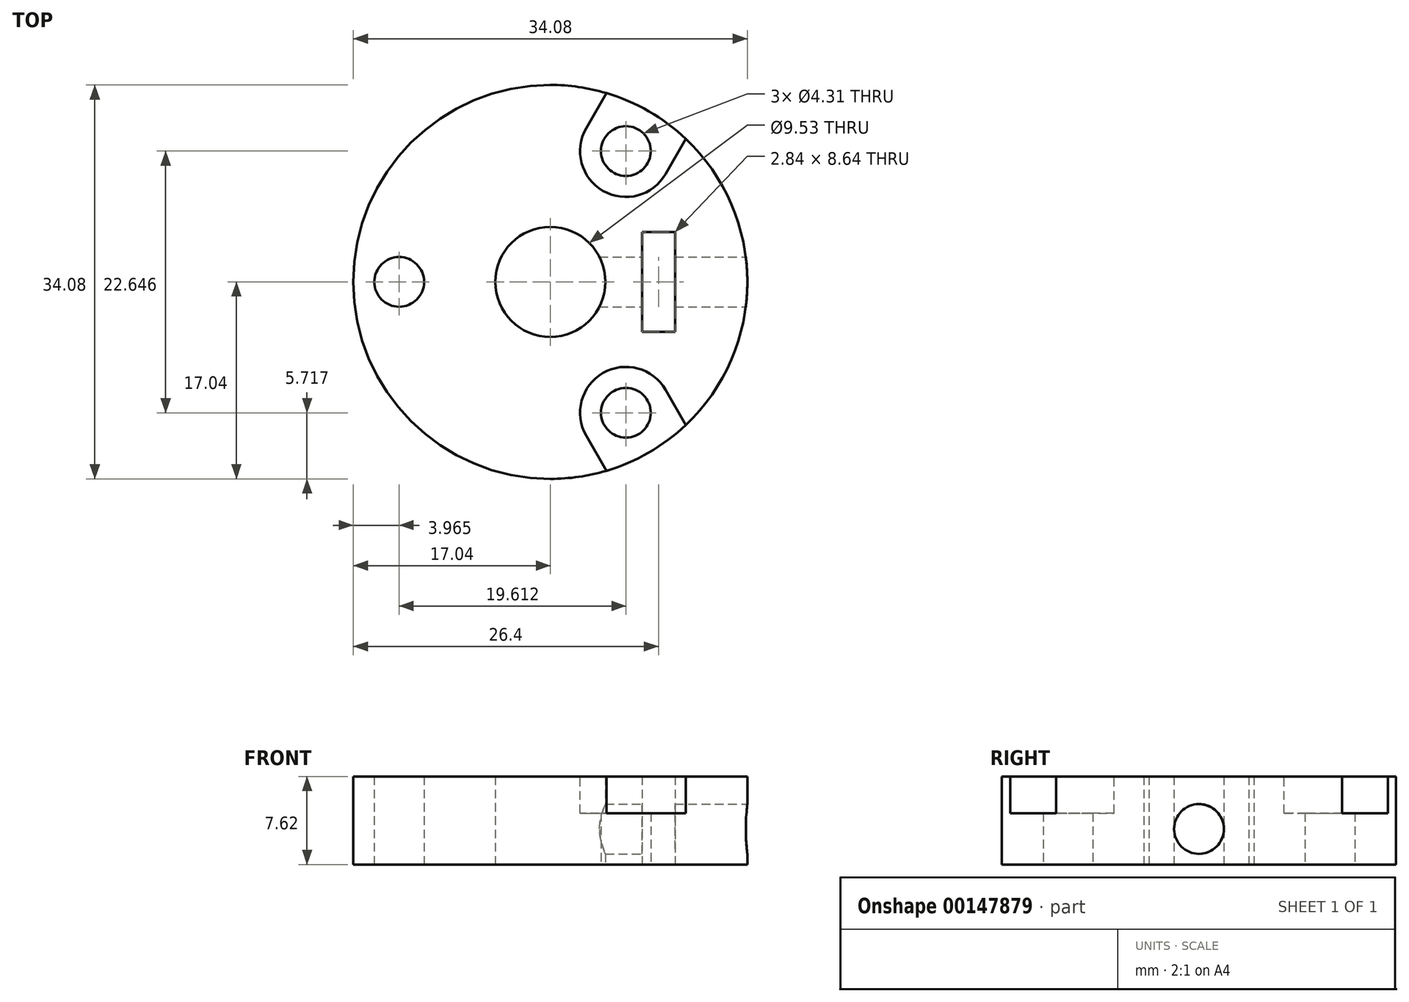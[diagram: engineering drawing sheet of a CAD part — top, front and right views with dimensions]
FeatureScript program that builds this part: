
annotation { "Feature Type Name" : "Feature", "Feature Type Description" : "" }
export const myFeature = defineFeature(function(context is Context, id is Id, definition is map)
    precondition{}
    {
        {
            var Q0;
            Q0=qCreatedBy(makeId("Top.planeOp"),FACE);
            var sketch = newSketch(context, id + "F0", { "sketchPlane" : qUnion([Q0])});
            skCircle(sketch, "E0", {"center": v(0, 0) * mm, "radius": 4.76 * mm});
            skCircle(sketch, "E1.cCircle", {"center": v(0, 0) * mm, "radius": 6.54 * mm, "construction": true});
            skLineSegment(sketch, "E1.0", {"start": v(6.54, 11.32) * mm, "end": v(6.54, -11.32) * mm, "construction": true});
            skLineSegment(sketch, "E1.1", {"start": v(6.54, -11.32) * mm, "end": v(-13.07, 0) * mm, "construction": true});
            skLineSegment(sketch, "E1.2", {"start": v(-13.07, 0) * mm, "end": v(6.54, 11.32) * mm, "construction": true});
            skCircle(sketch, "E2", {"center": v(-13.07, 0) * mm, "radius": 2.15 * mm});
            skCircle(sketch, "E3", {"center": v(6.54, -11.32) * mm, "radius": 2.15 * mm});
            skCircle(sketch, "E4", {"center": v(6.54, 11.32) * mm, "radius": 2.15 * mm});
            skLineSegment(sketch, "E5", {"start": v(4.76, 0) * mm, "end": v(7.94, 0) * mm, "construction": true});
            skLineSegment(sketch, "E6.bottom", {"start": v(7.94, -4.32) * mm, "end": v(10.78, -4.32) * mm});
            skLineSegment(sketch, "E6.top", {"start": v(7.94, 4.32) * mm, "end": v(10.78, 4.32) * mm});
            skLineSegment(sketch, "E6.left", {"start": v(7.94, -4.32) * mm, "end": v(7.94, 4.32) * mm});
            skLineSegment(sketch, "E6.right", {"start": v(10.78, -4.32) * mm, "end": v(10.78, 4.32) * mm});
            skCircle(sketch, "E7", {"center": v(6.54, -11.32) * mm, "radius": 7.14 * mm, "construction": true});
            skPoint(sketch, "E8", {"position": v(6.54, 0) * mm});
            skCircle(sketch, "E9", {"center": v(-13.07, 0) * mm, "radius": 3.97 * mm, "construction": true});
            skLineSegment(sketch, "E10.bottom", {"start": v(-17.04, -17.04) * mm, "end": v(17.04, -17.04) * mm});
            skLineSegment(sketch, "E10.top", {"start": v(-17.04, 17.04) * mm, "end": v(17.04, 17.04) * mm});
            skLineSegment(sketch, "E10.left", {"start": v(-17.04, -17.04) * mm, "end": v(-17.04, 17.04) * mm});
            skLineSegment(sketch, "E10.right", {"start": v(17.04, -17.04) * mm, "end": v(17.04, 17.04) * mm});
            skSolve(sketch);
        }
        {
            var Q0;
            Q0=qSketchRegion(id+"F0",true);
            extrude(context, id + "F1", {"entities" : qUnion([Q0]), "depth" : 7.62 * mm});
        }
        {
            var Q0;
            Q0=makeQuery(id+"F1.opExtrude","SWEPT_FACE",FACE,{"disambiguationData":[OSD([sQuery(id+"F0.wireOp",EDGE,"E10.right")])]});
            var sketch = newSketch(context, id + "F2", { "sketchPlane" : qUnion([Q0])});
            skCircle(sketch, "E11", {"center": v(0, 3.07) * mm, "radius": 2.15 * mm});
            skCircle(sketch, "E12.cCircle", {"center": v(0, 3.07) * mm, "radius": 3.94 * mm, "construction": true});
            skLineSegment(sketch, "E12.0", {"start": v(0, 7.62) * mm, "end": v(3.94, 5.35) * mm, "construction": true});
            skLineSegment(sketch, "E12.1", {"start": v(3.94, 5.35) * mm, "end": v(3.94, 0.8) * mm, "construction": true});
            skLineSegment(sketch, "E12.2", {"start": v(3.94, 0.8) * mm, "end": v(0, -1.47) * mm, "construction": true});
            skLineSegment(sketch, "E12.3", {"start": v(0, -1.47) * mm, "end": v(-3.94, 0.8) * mm, "construction": true});
            skLineSegment(sketch, "E12.4", {"start": v(-3.94, 0.8) * mm, "end": v(-3.94, 5.35) * mm, "construction": true});
            skLineSegment(sketch, "E12.5", {"start": v(-3.94, 5.35) * mm, "end": v(0, 7.62) * mm, "construction": true});
            skLineSegment(sketch, "E13", {"start": v(0, 7.62) * mm, "end": v(0, 3.07) * mm, "construction": true});
            skSolve(sketch);
        }
        {
            var Q0;
            Q0=qSketchRegion(id+"F2",true);
            var Q1;
            Q1=makeQuery(id+"F1.opExtrude","SWEPT_FACE",FACE,{"disambiguationData":[OSD([sQuery(id+"F0.wireOp",EDGE,"E0")])]});
            extrude(context, id + "F3", {"entities" : qUnion([Q0]), "operationType" : NewBodyOperationType.REMOVE, "endBound" : BoundingType.UP_TO_SURFACE, "oppositeDirection" : true, "endBoundEntityFace" : qUnion([Q1]), "depth" : 25.4 * mm});
        }
        {
            var Q0;
            Q0=makeQuery(id+"F1.opExtrude","SWEPT_EDGE",EDGE,{"disambiguationData":[OSD([sQuery(id+"F0.wireOp",EDGE,"E10.bottom"),sQuery(id+"F0.wireOp",EDGE,"E10.right")])]});
            var Q1;
            Q1=makeQuery(id+"F1.opExtrude","SWEPT_EDGE",EDGE,{"disambiguationData":[OSD([sQuery(id+"F0.wireOp",EDGE,"E10.top"),sQuery(id+"F0.wireOp",EDGE,"E10.right")])]});
            var Q2;
            Q2=makeQuery(id+"F1.opExtrude","SWEPT_EDGE",EDGE,{"disambiguationData":[OSD([sQuery(id+"F0.wireOp",EDGE,"E10.top"),sQuery(id+"F0.wireOp",EDGE,"E10.left")])]});
            var Q3;
            Q3=makeQuery(id+"F1.opExtrude","SWEPT_EDGE",EDGE,{"disambiguationData":[OSD([sQuery(id+"F0.wireOp",EDGE,"E10.bottom"),sQuery(id+"F0.wireOp",EDGE,"E10.left")])]});
            fillet(context, id + "F4", {"entities" : qUnion([Q0, Q1, Q2, Q3]), "radius" : 17.04 * mm, "tangentPropagation" : true, "allowEdgeOverflow" : false});
        }
        {
            var Q0;
            Q0=makeQuery(id+"F1.opExtrude","CAP_FACE",FACE,{"disambiguationData":[OSD([sQuery(id+"F0.wireOp",EDGE,"E0"),sQuery(id+"F0.wireOp",EDGE,"E2"),sQuery(id+"F0.wireOp",EDGE,"E3"),sQuery(id+"F0.wireOp",EDGE,"E4"),sQuery(id+"F0.wireOp",EDGE,"E6.bottom"),sQuery(id+"F0.wireOp",EDGE,"E6.top"),sQuery(id+"F0.wireOp",EDGE,"E6.left"),sQuery(id+"F0.wireOp",EDGE,"E6.right"),sQuery(id+"F0.wireOp",EDGE,"E10.bottom"),sQuery(id+"F0.wireOp",EDGE,"E10.top"),sQuery(id+"F0.wireOp",EDGE,"E10.left"),sQuery(id+"F0.wireOp",EDGE,"E10.right")])],"isStart":true});
            cPlane(context, id + "F5", {"entities" : qUnion([Q0]), "cplaneType" : CPlaneType.OFFSET, "offset" : 4.44 * mm, "oppositeDirection" : true, "width" : 152.4 * mm, "height" : 152.4 * mm});
        }
        {
            var Q0;
            Q0=makeQuery(id+"F1.opExtrude","CAP_FACE",FACE,{"disambiguationData":[OSD([sQuery(id+"F0.wireOp",EDGE,"E0"),sQuery(id+"F0.wireOp",EDGE,"emHaSGx0-YgNI-fRC0-JXiY-vh4g6PRLvdxu"),sQuery(id+"F0.wireOp",EDGE,"E2"),sQuery(id+"F0.wireOp",EDGE,"E3"),sQuery(id+"F0.wireOp",EDGE,"E4")])],"isStart":false});
            var sketch = newSketch(context, id + "F6", { "sketchPlane" : qUnion([Q0])});
            skLineSegment(sketch, "E14", {"start": v(0, 0) * mm, "end": v(6.54, 11.32) * mm, "construction": true});
            skLineSegment(sketch, "E15", {"start": v(0, 0) * mm, "end": v(6.54, -11.32) * mm, "construction": true});
            skLineSegment(sketch, "E16", {"start": v(0, 0) * mm, "end": v(-13.07, 0) * mm, "construction": true});
            skLineSegment(sketch, "E17.bottom", {"start": v(-17.04, 3.97) * mm, "end": v(-13.07, 3.97) * mm});
            skLineSegment(sketch, "E17.top", {"start": v(-17.04, -3.97) * mm, "end": v(-13.07, -3.97) * mm});
            skLineSegment(sketch, "E17.left", {"start": v(-17.04, 3.97) * mm, "end": v(-17.04, -3.97) * mm});
            skLineSegment(sketch, "E17.right", {"start": v(-13.07, 3.97) * mm, "end": v(-13.07, -3.97) * mm, "construction": true});
            skLineSegment(sketch, "E18.bottom", {"start": v(3.1, 13.3) * mm, "end": v(9.97, 9.34) * mm, "construction": true});
            skLineSegment(sketch, "E18.top", {"start": v(5.08, 16.74) * mm, "end": v(11.96, 12.78) * mm});
            skLineSegment(sketch, "E18.left", {"start": v(3.1, 13.3) * mm, "end": v(5.08, 16.74) * mm});
            skLineSegment(sketch, "E18.right", {"start": v(9.97, 9.34) * mm, "end": v(11.96, 12.78) * mm});
            skLineSegment(sketch, "E19.bottom", {"start": v(9.97, -9.34) * mm, "end": v(3.1, -13.3) * mm, "construction": true});
            skLineSegment(sketch, "E19.top", {"start": v(11.96, -12.78) * mm, "end": v(5.08, -16.74) * mm});
            skLineSegment(sketch, "E19.left", {"start": v(3.1, -13.3) * mm, "end": v(5.08, -16.74) * mm});
            skLineSegment(sketch, "E19.right", {"start": v(9.97, -9.34) * mm, "end": v(11.96, -12.78) * mm});
            skArc(sketch, "E20", {"start": v(9.97, -9.34) * mm, "mid": v(4.55, -7.89) * mm, "end": v(3.1, -13.3) * mm});
            skArc(sketch, "E21", {"start": v(3.1, 13.3) * mm, "mid": v(4.55, 7.89) * mm, "end": v(9.97, 9.34) * mm});
            skArc(sketch, "E22", {"start": v(-13.07, -3.97) * mm, "mid": v(-9.1, 0) * mm, "end": v(-13.07, 3.97) * mm});
            skSolve(sketch);
        }
        {
            var Q0;
            Q0=qSketchRegion(id+"F6",true);
            var Q1;
            Q1=qCreatedBy(id+"F5.planeOp",FACE);
            extrude(context, id + "F7", {"entities" : qUnion([Q0]), "operationType" : NewBodyOperationType.REMOVE, "endBound" : BoundingType.UP_TO_SURFACE, "oppositeDirection" : true, "endBoundEntityFace" : qUnion([Q1]), "depth" : 4.76 * mm});
        }
    });
